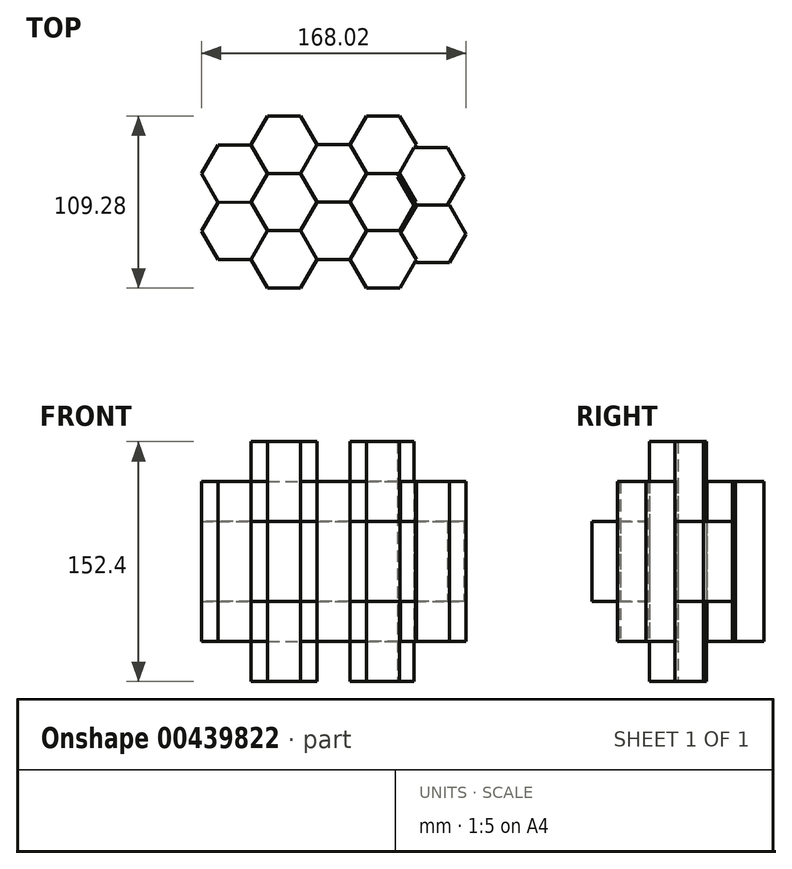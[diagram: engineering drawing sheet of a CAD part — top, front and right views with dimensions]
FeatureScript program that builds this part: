
annotation { "Feature Type Name" : "Feature", "Feature Type Description" : "" }
export const myFeature = defineFeature(function(context is Context, id is Id, definition is map)
    precondition{}
    {
        {
            var Q0;
            Q0=qCreatedBy(makeId("Top.planeOp"),FACE);
            var sketch = newSketch(context, id + "F0", { "sketchPlane" : qUnion([Q0])});
            skCircle(sketch, "E0.cCircle", {"center": v(-44.9, 25.32) * mm, "radius": 18.19 * mm, "construction": true});
            skLineSegment(sketch, "E0.0", {"start": v(-23.9, 25.34) * mm, "end": v(-34.38, 7.14) * mm});
            skLineSegment(sketch, "E0.1", {"start": v(-34.38, 7.14) * mm, "end": v(-55.38, 7.11) * mm});
            skLineSegment(sketch, "E0.2", {"start": v(-55.38, 7.11) * mm, "end": v(-65.9, 25.3) * mm});
            skLineSegment(sketch, "E0.3", {"start": v(-65.9, 25.3) * mm, "end": v(-55.42, 43.5) * mm});
            skLineSegment(sketch, "E0.4", {"start": v(-55.42, 43.5) * mm, "end": v(-34.42, 43.52) * mm});
            skLineSegment(sketch, "E0.5", {"start": v(-34.42, 43.52) * mm, "end": v(-23.9, 25.34) * mm});
            skPoint(sketch, "E0.0.midPoint", {"position": v(-29.14, 16.24) * mm});
            skCircle(sketch, "E1.cCircle", {"center": v(-13.42, 7.32) * mm, "radius": 18.19 * mm, "construction": true});
            skLineSegment(sketch, "E1.0", {"start": v(7.58, 7.35) * mm, "end": v(-2.9, -10.85) * mm});
            skLineSegment(sketch, "E1.1", {"start": v(-2.9, -10.85) * mm, "end": v(-23.9, -10.88) * mm});
            skLineSegment(sketch, "E1.2", {"start": v(-23.9, -10.88) * mm, "end": v(-34.42, 7.3) * mm});
            skLineSegment(sketch, "E1.3", {"start": v(-34.42, 7.3) * mm, "end": v(-23.94, 25.5) * mm});
            skLineSegment(sketch, "E1.4", {"start": v(-23.94, 25.5) * mm, "end": v(-2.94, 25.53) * mm});
            skLineSegment(sketch, "E1.5", {"start": v(-2.94, 25.53) * mm, "end": v(7.58, 7.35) * mm});
            skPoint(sketch, "E1.0.midPoint", {"position": v(2.34, -1.75) * mm});
            skCircle(sketch, "E2.cCircle", {"center": v(-44.9, -11.05) * mm, "radius": 18.19 * mm, "construction": true});
            skLineSegment(sketch, "E2.0", {"start": v(-23.9, -11.02) * mm, "end": v(-34.38, -29.22) * mm});
            skLineSegment(sketch, "E2.1", {"start": v(-34.38, -29.22) * mm, "end": v(-55.38, -29.25) * mm});
            skLineSegment(sketch, "E2.2", {"start": v(-55.38, -29.25) * mm, "end": v(-65.9, -11.07) * mm});
            skLineSegment(sketch, "E2.3", {"start": v(-65.9, -11.07) * mm, "end": v(-55.42, 7.13) * mm});
            skLineSegment(sketch, "E2.4", {"start": v(-55.42, 7.13) * mm, "end": v(-34.42, 7.16) * mm});
            skLineSegment(sketch, "E2.5", {"start": v(-34.42, 7.16) * mm, "end": v(-23.9, -11.02) * mm});
            skPoint(sketch, "E2.0.midPoint", {"position": v(-29.14, -20.12) * mm});
            skCircle(sketch, "E3.cCircle", {"center": v(-13.42, 43.7) * mm, "radius": 18.19 * mm, "construction": true});
            skLineSegment(sketch, "E3.0", {"start": v(7.58, 43.73) * mm, "end": v(-2.9, 25.53) * mm});
            skLineSegment(sketch, "E3.1", {"start": v(-2.9, 25.53) * mm, "end": v(-23.9, 25.5) * mm});
            skLineSegment(sketch, "E3.2", {"start": v(-23.9, 25.5) * mm, "end": v(-34.42, 43.68) * mm});
            skLineSegment(sketch, "E3.3", {"start": v(-34.42, 43.68) * mm, "end": v(-23.94, 61.88) * mm});
            skLineSegment(sketch, "E3.4", {"start": v(-23.94, 61.88) * mm, "end": v(-2.94, 61.9) * mm});
            skLineSegment(sketch, "E3.5", {"start": v(-2.94, 61.9) * mm, "end": v(7.58, 43.73) * mm});
            skPoint(sketch, "E3.0.midPoint", {"position": v(2.34, 34.63) * mm});
            skCircle(sketch, "E4.cCircle", {"center": v(-13.42, -29.13) * mm, "radius": 18.19 * mm, "construction": true});
            skLineSegment(sketch, "E4.0", {"start": v(7.58, -29.1) * mm, "end": v(-2.9, -47.3) * mm});
            skLineSegment(sketch, "E4.1", {"start": v(-2.9, -47.3) * mm, "end": v(-23.9, -47.33) * mm});
            skLineSegment(sketch, "E4.2", {"start": v(-23.9, -47.33) * mm, "end": v(-34.42, -29.16) * mm});
            skLineSegment(sketch, "E4.3", {"start": v(-34.42, -29.16) * mm, "end": v(-23.94, -10.96) * mm});
            skLineSegment(sketch, "E4.4", {"start": v(-23.94, -10.96) * mm, "end": v(-2.94, -10.93) * mm});
            skLineSegment(sketch, "E4.5", {"start": v(-2.94, -10.93) * mm, "end": v(7.58, -29.1) * mm});
            skPoint(sketch, "E4.0.midPoint", {"position": v(2.34, -38.2) * mm});
            skCircle(sketch, "E5.cCircle", {"center": v(18.06, 25.55) * mm, "radius": 18.19 * mm, "construction": true});
            skLineSegment(sketch, "E5.0", {"start": v(39.07, 25.58) * mm, "end": v(28.59, 7.37) * mm});
            skLineSegment(sketch, "E5.1", {"start": v(28.59, 7.37) * mm, "end": v(7.58, 7.35) * mm});
            skLineSegment(sketch, "E5.2", {"start": v(7.58, 7.35) * mm, "end": v(-2.94, 25.53) * mm});
            skLineSegment(sketch, "E5.3", {"start": v(-2.94, 25.53) * mm, "end": v(7.54, 43.73) * mm});
            skLineSegment(sketch, "E5.4", {"start": v(7.54, 43.73) * mm, "end": v(28.54, 43.75) * mm});
            skLineSegment(sketch, "E5.5", {"start": v(28.54, 43.75) * mm, "end": v(39.07, 25.58) * mm});
            skPoint(sketch, "E5.0.midPoint", {"position": v(33.83, 16.48) * mm});
            skCircle(sketch, "E6.cCircle", {"center": v(18, -11.02) * mm, "radius": 18.19 * mm, "construction": true});
            skLineSegment(sketch, "E6.0", {"start": v(39, -11) * mm, "end": v(28.52, -29.2) * mm});
            skLineSegment(sketch, "E6.1", {"start": v(28.52, -29.2) * mm, "end": v(7.52, -29.22) * mm});
            skLineSegment(sketch, "E6.2", {"start": v(7.52, -29.22) * mm, "end": v(-3, -11.05) * mm});
            skLineSegment(sketch, "E6.3", {"start": v(-3, -11.05) * mm, "end": v(7.48, 7.16) * mm});
            skLineSegment(sketch, "E6.4", {"start": v(7.48, 7.16) * mm, "end": v(28.48, 7.18) * mm});
            skLineSegment(sketch, "E6.5", {"start": v(28.48, 7.18) * mm, "end": v(39, -11) * mm});
            skPoint(sketch, "E6.0.midPoint", {"position": v(33.76, -20.1) * mm});
            skCircle(sketch, "E7.cCircle", {"center": v(49.4, 7.35) * mm, "radius": 18.19 * mm, "construction": true});
            skLineSegment(sketch, "E7.0", {"start": v(70.4, 7.37) * mm, "end": v(59.92, -10.83) * mm});
            skLineSegment(sketch, "E7.1", {"start": v(59.92, -10.83) * mm, "end": v(38.92, -10.85) * mm});
            skLineSegment(sketch, "E7.2", {"start": v(38.92, -10.85) * mm, "end": v(28.4, 7.32) * mm});
            skLineSegment(sketch, "E7.3", {"start": v(28.4, 7.32) * mm, "end": v(38.88, 25.53) * mm});
            skLineSegment(sketch, "E7.4", {"start": v(38.88, 25.53) * mm, "end": v(59.88, 25.55) * mm});
            skLineSegment(sketch, "E7.5", {"start": v(59.88, 25.55) * mm, "end": v(70.4, 7.37) * mm});
            skPoint(sketch, "E7.0.midPoint", {"position": v(65.16, -1.73) * mm});
            skCircle(sketch, "E8.cCircle", {"center": v(49.53, 43.74) * mm, "radius": 18.19 * mm, "construction": true});
            skLineSegment(sketch, "E8.0", {"start": v(70.53, 43.77) * mm, "end": v(60.05, 25.57) * mm});
            skLineSegment(sketch, "E8.1", {"start": v(60.05, 25.57) * mm, "end": v(39.05, 25.54) * mm});
            skLineSegment(sketch, "E8.2", {"start": v(39.05, 25.54) * mm, "end": v(28.52, 43.72) * mm});
            skLineSegment(sketch, "E8.3", {"start": v(28.52, 43.72) * mm, "end": v(39, 61.92) * mm});
            skLineSegment(sketch, "E8.4", {"start": v(39, 61.92) * mm, "end": v(60, 61.94) * mm});
            skLineSegment(sketch, "E8.5", {"start": v(60, 61.94) * mm, "end": v(70.53, 43.77) * mm});
            skPoint(sketch, "E8.0.midPoint", {"position": v(65.29, 34.67) * mm});
            skCircle(sketch, "E9.cCircle", {"center": v(49.55, -29.14) * mm, "radius": 18.19 * mm, "construction": true});
            skLineSegment(sketch, "E9.0", {"start": v(70.55, -29.11) * mm, "end": v(60.07, -47.31) * mm});
            skLineSegment(sketch, "E9.1", {"start": v(60.07, -47.31) * mm, "end": v(39.07, -47.34) * mm});
            skLineSegment(sketch, "E9.2", {"start": v(39.07, -47.34) * mm, "end": v(28.54, -29.16) * mm});
            skLineSegment(sketch, "E9.3", {"start": v(28.54, -29.16) * mm, "end": v(39.02, -10.96) * mm});
            skLineSegment(sketch, "E9.4", {"start": v(39.02, -10.96) * mm, "end": v(60.03, -10.94) * mm});
            skLineSegment(sketch, "E9.5", {"start": v(60.03, -10.94) * mm, "end": v(70.55, -29.11) * mm});
            skPoint(sketch, "E9.0.midPoint", {"position": v(65.31, -38.21) * mm});
            skCircle(sketch, "E10.cCircle", {"center": v(79.73, 23.59) * mm, "radius": 18.19 * mm, "construction": true});
            skLineSegment(sketch, "E10.0", {"start": v(100.74, 23.61) * mm, "end": v(90.26, 5.4) * mm});
            skLineSegment(sketch, "E10.1", {"start": v(90.26, 5.4) * mm, "end": v(69.26, 5.38) * mm});
            skLineSegment(sketch, "E10.2", {"start": v(69.26, 5.38) * mm, "end": v(58.73, 23.56) * mm});
            skLineSegment(sketch, "E10.3", {"start": v(58.73, 23.56) * mm, "end": v(69.21, 41.76) * mm});
            skLineSegment(sketch, "E10.4", {"start": v(69.21, 41.76) * mm, "end": v(90.21, 41.79) * mm});
            skLineSegment(sketch, "E10.5", {"start": v(90.21, 41.79) * mm, "end": v(100.74, 23.61) * mm});
            skPoint(sketch, "E10.0.midPoint", {"position": v(95.5, 14.5) * mm});
            skCircle(sketch, "E11.cCircle", {"center": v(81.11, -12.96) * mm, "radius": 18.19 * mm, "construction": true});
            skLineSegment(sketch, "E11.0", {"start": v(102.12, -12.93) * mm, "end": v(91.64, -31.13) * mm});
            skLineSegment(sketch, "E11.1", {"start": v(91.64, -31.13) * mm, "end": v(70.63, -31.16) * mm});
            skLineSegment(sketch, "E11.2", {"start": v(70.63, -31.16) * mm, "end": v(60.11, -12.98) * mm});
            skLineSegment(sketch, "E11.3", {"start": v(60.11, -12.98) * mm, "end": v(70.6, 5.22) * mm});
            skLineSegment(sketch, "E11.4", {"start": v(70.6, 5.22) * mm, "end": v(91.6, 5.24) * mm});
            skLineSegment(sketch, "E11.5", {"start": v(91.6, 5.24) * mm, "end": v(102.12, -12.93) * mm});
            skPoint(sketch, "E11.0.midPoint", {"position": v(96.88, -22.03) * mm});
            skSolve(sketch);
        }
        {
            var Q0;
            {var subQ0=sQuery(id+"F0.wireOp",EDGE,"E0.5");var subQ1=sQuery(id+"F0.wireOp",EDGE,"E0.0");var subQ2=makeQuery(id+"F0.imprint","INTERSECT",VERTEX,{"derivedFrom":[subQ1,subQ0]});Q0=makeQuery(id+"F0.imprint","IMPRINT",FACE,{"disambiguationData":[TD([[makeQuery(id+"F0.imprint","IMPRINT",EDGE,{"disambiguationData":[TD([[subQ2,-1.0]])],"derivedFrom":subQ1}),-1.0]])]});}
            var Q1;
            {var subQ0=sQuery(id+"F0.wireOp",EDGE,"E0.2");var subQ1=sQuery(id+"F0.wireOp",EDGE,"E0.1");var subQ2=makeQuery(id+"F0.imprint","INTERSECT",VERTEX,{"derivedFrom":[subQ1,subQ0]});Q1=makeQuery(id+"F0.imprint","IMPRINT",FACE,{"disambiguationData":[TD([[makeQuery(id+"F0.imprint","IMPRINT",EDGE,{"disambiguationData":[TD([[subQ2,1.0]])],"derivedFrom":subQ1}),-1.0]])]});}
            var Q2;
            {var subQ1=sQuery(id+"F0.wireOp",EDGE,"E2.0");Q2=makeQuery(id+"F0.imprint","IMPRINT",FACE,{"disambiguationData":[TD([[makeQuery(id+"F0.imprint","IMPRINT",EDGE,{"derivedFrom":subQ1}),-1.0]])]});}
            var Q3;
            {var subQ0=sQuery(id+"F0.wireOp",EDGE,"E3.0");Q3=makeQuery(id+"F0.imprint","IMPRINT",FACE,{"disambiguationData":[TD([[makeQuery(id+"F0.imprint","IMPRINT",EDGE,{"derivedFrom":subQ0}),-1.0]])]});}
            var Q4;
            {var subQ0=sQuery(id+"F0.wireOp",EDGE,"E4.5");Q4=makeQuery(id+"F0.imprint","IMPRINT",FACE,{"disambiguationData":[TD([[makeQuery(id+"F0.imprint","IMPRINT",EDGE,{"derivedFrom":subQ0}),-1.0]])]});}
            var Q5;
            {var subQ0=sQuery(id+"F0.wireOp",EDGE,"E5.5");Q5=makeQuery(id+"F0.imprint","IMPRINT",FACE,{"disambiguationData":[TD([[makeQuery(id+"F0.imprint","IMPRINT",EDGE,{"derivedFrom":subQ0}),-1.0]])]});}
            var Q6;
            {var subQ0=sQuery(id+"F0.wireOp",EDGE,"E8.1");var subQ1=sQuery(id+"F0.wireOp",EDGE,"E8.0");var subQ2=makeQuery(id+"F0.imprint","INTERSECT",VERTEX,{"derivedFrom":[subQ1,subQ0]});Q6=makeQuery(id+"F0.imprint","IMPRINT",FACE,{"disambiguationData":[TD([[makeQuery(id+"F0.imprint","IMPRINT",EDGE,{"disambiguationData":[TD([[subQ2,1.0]])],"derivedFrom":subQ1}),-1.0]])]});}
            var Q7;
            {var subQ0=sQuery(id+"F0.wireOp",EDGE,"E9.5");var subQ1=sQuery(id+"F0.wireOp",EDGE,"E9.0");var subQ2=makeQuery(id+"F0.imprint","INTERSECT",VERTEX,{"derivedFrom":[subQ1,subQ0]});Q7=makeQuery(id+"F0.imprint","IMPRINT",FACE,{"disambiguationData":[TD([[makeQuery(id+"F0.imprint","IMPRINT",EDGE,{"disambiguationData":[TD([[subQ2,-1.0]])],"derivedFrom":subQ1}),-1.0]])]});}
            var Q8;
            {var subQ0=sQuery(id+"F0.wireOp",EDGE,"E0.3");Q8=makeQuery(id+"F0.imprint","IMPRINT",FACE,{"disambiguationData":[TD([[makeQuery(id+"F0.imprint","IMPRINT",EDGE,{"derivedFrom":subQ0}),-1.0]])]});}
            var Q9;
            {var subQ9=sQuery(id+"F0.wireOp",EDGE,"E3.0");Q9=makeQuery(id+"F0.imprint","IMPRINT",FACE,{"disambiguationData":[TD([[makeQuery(id+"F0.imprint","IMPRINT",EDGE,{"derivedFrom":subQ9}),1.0]])]});}
            var Q10;
            {var subQ8=sQuery(id+"F0.wireOp",EDGE,"E7.5");Q10=makeQuery(id+"F0.imprint","IMPRINT",FACE,{"disambiguationData":[TD([[makeQuery(id+"F0.imprint","IMPRINT",EDGE,{"derivedFrom":subQ8}),1.0]])]});}
            var Q11;
            {var subQ0=sQuery(id+"F0.wireOp",EDGE,"E9.1");Q11=makeQuery(id+"F0.imprint","IMPRINT",FACE,{"disambiguationData":[TD([[makeQuery(id+"F0.imprint","IMPRINT",EDGE,{"derivedFrom":subQ0}),-1.0]])]});}
            var Q12;
            {var subQ4=sQuery(id+"F0.wireOp",EDGE,"E2.0");Q12=makeQuery(id+"F0.imprint","IMPRINT",FACE,{"disambiguationData":[TD([[makeQuery(id+"F0.imprint","IMPRINT",EDGE,{"derivedFrom":subQ4}),1.0]])]});}
            extrude(context, id + "F1", {"entities" : qUnion([Q0, Q1, Q2, Q3, Q4, Q5, Q6, Q7, Q8, Q9, Q10, Q11, Q12]), "depth" : 25.4 * mm, "hasSecondDirection" : true, "secondDirectionOppositeDirection" : true, "secondDirectionDepth" : 25.4 * mm});
        }
        {
            var Q0;
            {var subQ0=sQuery(id+"F0.wireOp",EDGE,"E2.2");Q0=makeQuery(id+"F0.imprint","IMPRINT",FACE,{"disambiguationData":[TD([[makeQuery(id+"F0.imprint","IMPRINT",EDGE,{"derivedFrom":subQ0}),-1.0]])]});}
            var Q1;
            {var subQ0=sQuery(id+"F0.wireOp",EDGE,"E4.5");Q1=makeQuery(id+"F0.imprint","IMPRINT",FACE,{"disambiguationData":[TD([[makeQuery(id+"F0.imprint","IMPRINT",EDGE,{"derivedFrom":subQ0}),1.0]])]});}
            var Q2;
            Q2=makeQuery(id+"F0.imprint","IMPRINT",FACE,{"disambiguationData":[TD([[makeQuery(id+"F0.imprint","IMPRINT",EDGE,{"derivedFrom":sQuery(id+"F0.wireOp",EDGE,"E11.0")}),-1.0]])]});
            var Q3;
            {var subQ8=sQuery(id+"F0.wireOp",EDGE,"E5.5");Q3=makeQuery(id+"F0.imprint","IMPRINT",FACE,{"disambiguationData":[TD([[makeQuery(id+"F0.imprint","IMPRINT",EDGE,{"derivedFrom":subQ8}),1.0]])]});}
            var Q4;
            {var subQ0=sQuery(id+"F0.wireOp",EDGE,"E3.2");Q4=makeQuery(id+"F0.imprint","IMPRINT",FACE,{"disambiguationData":[TD([[makeQuery(id+"F0.imprint","IMPRINT",EDGE,{"derivedFrom":subQ0}),-1.0]])]});}
            extrude(context, id + "F2", {"entities" : qUnion([Q0, Q1, Q2, Q3, Q4]), "depth" : 50.8 * mm, "hasSecondDirection" : true, "secondDirectionOppositeDirection" : true, "secondDirectionDepth" : 50.8 * mm});
        }
        {
            var Q0;
            Q0=makeQuery(id+"F0.imprint","IMPRINT",FACE,{"disambiguationData":[TD([[makeQuery(id+"F0.imprint","IMPRINT",EDGE,{"derivedFrom":sQuery(id+"F0.wireOp",EDGE,"E1.0")}),-1.0]])]});
            var Q1;
            {var subQ0=sQuery(id+"F0.wireOp",EDGE,"E7.1");Q1=makeQuery(id+"F0.imprint","IMPRINT",FACE,{"disambiguationData":[TD([[makeQuery(id+"F0.imprint","IMPRINT",EDGE,{"derivedFrom":subQ0}),-1.0]])]});}
            extrude(context, id + "F3", {"entities" : qUnion([Q0, Q1]), "depth" : 76.2 * mm, "hasSecondDirection" : true, "secondDirectionOppositeDirection" : true, "secondDirectionDepth" : 76.2 * mm});
        }
    });
